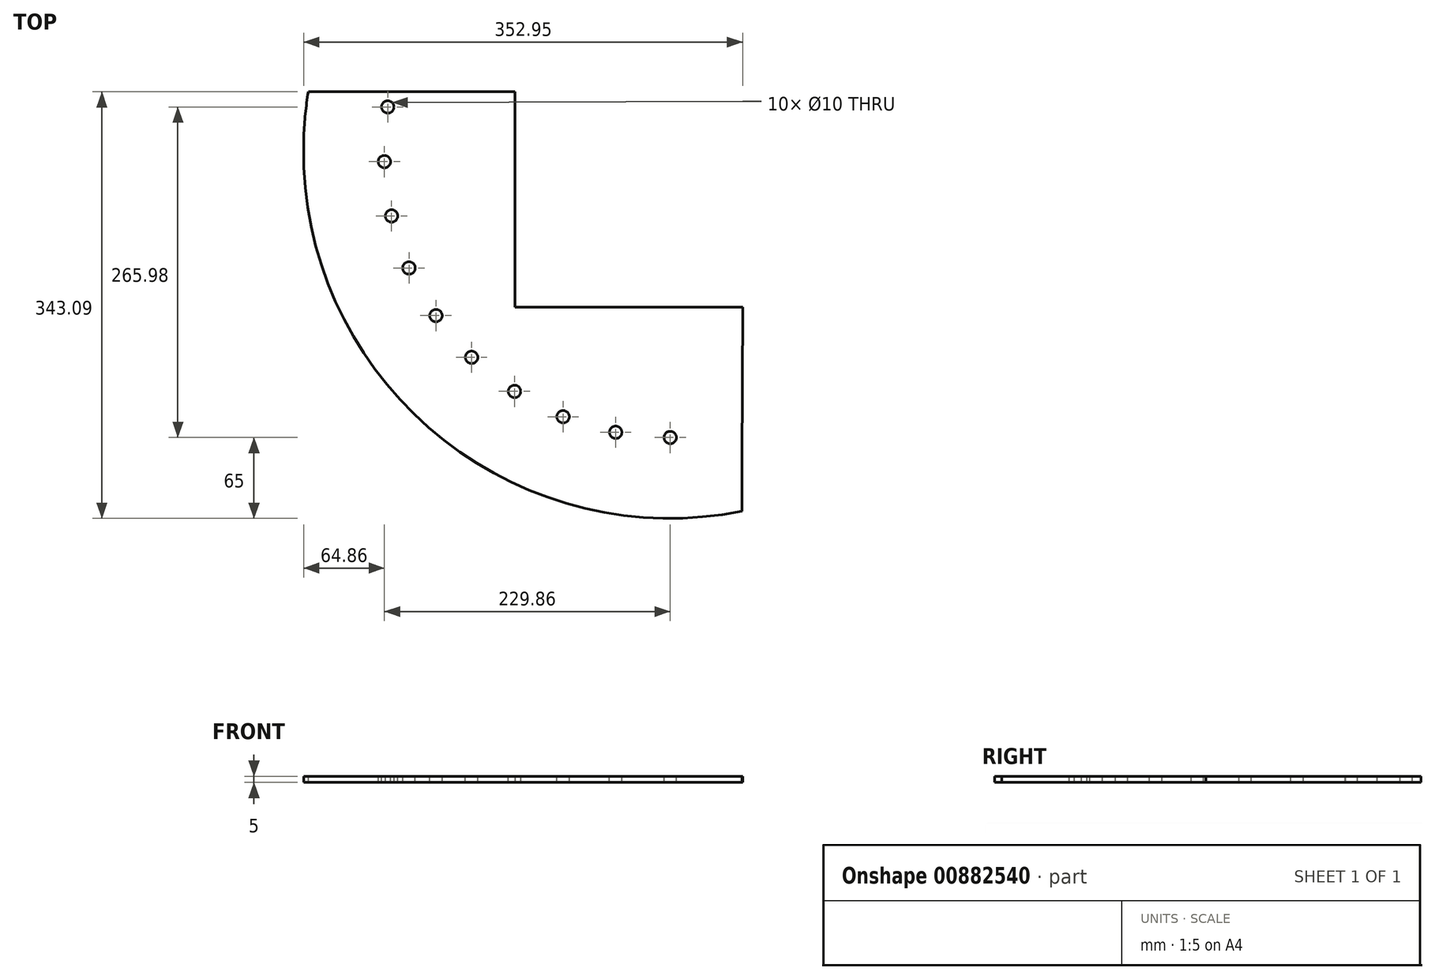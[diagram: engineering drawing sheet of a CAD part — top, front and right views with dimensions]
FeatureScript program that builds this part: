
annotation { "Feature Type Name" : "Feature", "Feature Type Description" : "" }
export const myFeature = defineFeature(function(context is Context, id is Id, definition is map)
    precondition{}
    {
        {
            var Q0;
            Q0=qCreatedBy(makeId("Top.planeOp"),FACE);
            var sketch = newSketch(context, id + "F0", { "sketchPlane" : qUnion([Q0])});
            skLineSegment(sketch, "E0.bottom", {"start": v(125, -125) * mm, "end": v(-125, -125) * mm});
            skLineSegment(sketch, "E0.top", {"start": v(125, 125) * mm, "end": v(-125, 125) * mm});
            skLineSegment(sketch, "E0.left", {"start": v(125, -125) * mm, "end": v(125, 125) * mm});
            skLineSegment(sketch, "E0.right", {"start": v(-125, -125) * mm, "end": v(-125, 125) * mm});
            skPoint(sketch, "E0.middle", {"position": v(0, 0) * mm});
            skLineSegment(sketch, "E1", {"start": v(0, 0) * mm, "end": v(-125, 0) * mm, "construction": true});
            skLineSegment(sketch, "E2.bottom", {"start": v(-349.96, 0) * mm, "end": v(0, 0) * mm});
            skLineSegment(sketch, "E2.left", {"start": v(-349.96, 0) * mm, "end": v(-349.96, 125) * mm});
            skLineSegment(sketch, "E2.right", {"start": v(125, 0) * mm, "end": v(125, 125) * mm});
            skLineSegment(sketch, "E3.MirrorCS", {"start": v(-349.96, 0) * mm, "end": v(-349.96, -249.62) * mm});
            skLineSegment(sketch, "E4.MirrorCS", {"start": v(-349.96, -249.62) * mm, "end": v(125, -249.62) * mm});
            skLineSegment(sketch, "E5.MirrorCS", {"start": v(125, 0) * mm, "end": v(125, -249.62) * mm});
            skLineSegment(sketch, "E6", {"start": v(-349.96, 125) * mm, "end": v(125, 125) * mm});
            skPoint(sketch, "E2.top.start.orphan", {"position": v(-349.96, 249.62) * mm});
            skPoint(sketch, "E7.orphan", {"position": v(125, 249.62) * mm});
            skLineSegment(sketch, "E8", {"start": v(-349.96, 29.15) * mm, "end": v(-125, 29.15) * mm});
            skLineSegment(sketch, "E9", {"start": v(-349.96, -249.62) * mm, "end": v(-349.96, -298.58) * mm});
            skLineSegment(sketch, "E10", {"start": v(-349.96, -298.58) * mm, "end": v(124.79, -298.58) * mm});
            skLineSegment(sketch, "E11", {"start": v(124.79, -298.58) * mm, "end": v(125, -249.62) * mm});
            skLineSegment(sketch, "E12", {"start": v(-294.72, 29.15) * mm, "end": v(-294.72, -298.58) * mm});
            skLineSegment(sketch, "E13", {"start": v(-294.72, 29.15) * mm, "end": v(-294.72, 125) * mm});
            skLineSegment(sketch, "E14", {"start": v(-294.72, 125) * mm, "end": v(-294.72, 148.87) * mm});
            skLineSegment(sketch, "E15", {"start": v(-294.72, 148.87) * mm, "end": v(-125.13, 148.87) * mm});
            skLineSegment(sketch, "E16", {"start": v(-125.13, 148.87) * mm, "end": v(-125, 125) * mm});
            skSolve(sketch);
        }
        {
            var Q0;
            {var subQ0=sQuery(id+"F0.wireOp",EDGE,"E8");var subQ1=sQuery(id+"F0.wireOp",EDGE,"E0.right");var subQ2=makeQuery(id+"F0.imprint","INTERSECT",VERTEX,{"derivedFrom":[subQ1,subQ0]});Q0=makeQuery(id+"F0.imprint","IMPRINT",FACE,{"disambiguationData":[TD([[makeQuery(id+"F0.imprint","IMPRINT",EDGE,{"disambiguationData":[TD([[subQ2,1.0]])],"derivedFrom":subQ1}),1.0]])]});}
            var Q1;
            {var subQ5=sQuery(id+"F0.wireOp",EDGE,"E0.bottom");Q1=makeQuery(id+"F0.imprint","IMPRINT",FACE,{"disambiguationData":[TD([[makeQuery(id+"F0.imprint","IMPRINT",EDGE,{"derivedFrom":subQ5}),1.0]])]});}
            var Q2;
            {var subQ0=sQuery(id+"F0.wireOp",EDGE,"E11");Q2=makeQuery(id+"F0.imprint","IMPRINT",FACE,{"disambiguationData":[TD([[makeQuery(id+"F0.imprint","IMPRINT",EDGE,{"derivedFrom":subQ0}),1.0]])]});}
            var Q3;
            {var subQ4=sQuery(id+"F0.wireOp",EDGE,"E6");var subQ5=sQuery(id+"F0.wireOp",EDGE,"E0.right");var subQ6=makeQuery(id+"F0.imprint","INTERSECT",VERTEX,{"derivedFrom":[subQ5,subQ4]});Q3=makeQuery(id+"F0.imprint","IMPRINT",FACE,{"disambiguationData":[TD([[makeQuery(id+"F0.imprint","IMPRINT",EDGE,{"disambiguationData":[TD([[subQ6,1.0]])],"derivedFrom":subQ5}),1.0]])]});}
            var Q4;
            {var subQ2=sQuery(id+"F0.wireOp",EDGE,"E14");Q4=makeQuery(id+"F0.imprint","IMPRINT",FACE,{"disambiguationData":[TD([[makeQuery(id+"F0.imprint","IMPRINT",EDGE,{"derivedFrom":subQ2}),-1.0]])]});}
            extrude(context, id + "F1", {"entities" : qUnion([Q0, Q1, Q2, Q3, Q4]), "depth" : 5 * mm, "offsetDistance" : 25 * mm});
        }
        {
            var Q0;
            Q0=makeQuery(id+"F1.opExtrude","CAP_FACE",FACE,{"disambiguationData":[OSD([sQuery(id+"F0.wireOp",EDGE,"E0.bottom"),sQuery(id+"F0.wireOp",EDGE,"E0.top"),sQuery(id+"F0.wireOp",EDGE,"E0.left"),sQuery(id+"F0.wireOp",EDGE,"E0.right"),sQuery(id+"F0.wireOp",EDGE,"E2.top"),sQuery(id+"F0.wireOp",EDGE,"E2.left"),sQuery(id+"F0.wireOp",EDGE,"E2.right"),sQuery(id+"F0.wireOp",EDGE,"E3.MirrorCS"),sQuery(id+"F0.wireOp",EDGE,"E4.MirrorCS"),sQuery(id+"F0.wireOp",EDGE,"E5.MirrorCS")])],"isStart":false});
            var sketch = newSketch(context, id + "F2", { "sketchPlane" : qUnion([Q0])});
            skCircle(sketch, "E17", {"center": v(0, 0) * mm, "radius": 270 * mm});
            skCircle(sketch, "E18", {"center": v(0, 0) * mm, "radius": 190 * mm});
            skLineSegment(sketch, "E19", {"start": v(0, 0) * mm, "end": v(-270, 0) * mm, "construction": true});
            skCircle(sketch, "E20", {"center": v(0, 0) * mm, "radius": 230 * mm, "construction": true});
            skCircle(sketch, "E21", {"center": v(-216.13, 78.66) * mm, "radius": 40 * mm});
            skCircle(sketch, "E22", {"center": v(0, -230) * mm, "radius": 40 * mm});
            skLineSegment(sketch, "E23", {"start": v(-216.13, 78.66) * mm, "end": v(0, 0) * mm, "construction": true});
            skLineSegment(sketch, "E24", {"start": v(0, 0) * mm, "end": v(0, -230) * mm, "construction": true});
            skCircle(sketch, "E25", {"center": v(-216.13, 78.66) * mm, "radius": 5 * mm});
            skCircle(sketch, "E26.1.0", {"center": v(-227.17, 35.98) * mm, "radius": 5 * mm});
            skCircle(sketch, "E26.2.0", {"center": v(-229.86, -8.03) * mm, "radius": 5 * mm});
            skCircle(sketch, "E26.3.0", {"center": v(-224.1, -51.74) * mm, "radius": 5 * mm});
            skCircle(sketch, "E26.4.0", {"center": v(-210.12, -93.55) * mm, "radius": 5 * mm});
            skCircle(sketch, "E26.5.0", {"center": v(-188.4, -131.92) * mm, "radius": 5 * mm});
            skCircle(sketch, "E26.6.0", {"center": v(-159.77, -165.45) * mm, "radius": 5 * mm});
            skCircle(sketch, "E26.7.0", {"center": v(-125.27, -192.9) * mm, "radius": 5 * mm});
            skCircle(sketch, "E26.8.0", {"center": v(-86.16, -213.25) * mm, "radius": 5 * mm});
            skCircle(sketch, "E26.9.0", {"center": v(-43.89, -225.77) * mm, "radius": 5 * mm});
            skCircle(sketch, "E26.10.0", {"center": v(0, -230) * mm, "radius": 5 * mm});
            skLineSegment(sketch, "E26.anchor1", {"start": v(0, 0) * mm, "end": v(-216.13, 78.66) * mm, "construction": true});
            skSolve(sketch);
        }
        {
            var Q0;
            Q0=makeQuery(id+"F2.imprint","IMPRINT",FACE,{"disambiguationData":[TD([[makeQuery(id+"F2.imprint","IMPRINT",EDGE,{"derivedFrom":sQuery(id+"F2.wireOp",EDGE,"E26.10.0")}),1.0]])]});
            var Q1;
            {var subQ0=sQuery(id+"F2.wireOp",EDGE,"E26.9.0");var subQ1=sQuery(id+"F2.wireOp",EDGE,"E22");var subQ2=makeQuery(id+"F2.imprint","INTERSECT",VERTEX,{"disambiguationData":[OD(0.0)],"derivedFrom":[subQ1,subQ0]});Q1=makeQuery(id+"F2.imprint","IMPRINT",FACE,{"disambiguationData":[TD([[makeQuery(id+"F2.imprint","IMPRINT",EDGE,{"disambiguationData":[TD([[subQ2,-1.0]])],"derivedFrom":subQ1}),-1.0]])]});}
            var Q2;
            Q2=makeQuery(id+"F2.imprint","IMPRINT",FACE,{"disambiguationData":[TD([[makeQuery(id+"F2.imprint","IMPRINT",EDGE,{"derivedFrom":sQuery(id+"F2.wireOp",EDGE,"E26.8.0")}),1.0]])]});
            var Q3;
            Q3=makeQuery(id+"F2.imprint","IMPRINT",FACE,{"disambiguationData":[TD([[makeQuery(id+"F2.imprint","IMPRINT",EDGE,{"derivedFrom":sQuery(id+"F2.wireOp",EDGE,"E26.7.0")}),1.0]])]});
            var Q4;
            Q4=makeQuery(id+"F2.imprint","IMPRINT",FACE,{"disambiguationData":[TD([[makeQuery(id+"F2.imprint","IMPRINT",EDGE,{"derivedFrom":sQuery(id+"F2.wireOp",EDGE,"E26.5.0")}),1.0]])]});
            var Q5;
            Q5=makeQuery(id+"F2.imprint","IMPRINT",FACE,{"disambiguationData":[TD([[makeQuery(id+"F2.imprint","IMPRINT",EDGE,{"derivedFrom":sQuery(id+"F2.wireOp",EDGE,"E26.6.0")}),1.0]])]});
            var Q6;
            Q6=makeQuery(id+"F2.imprint","IMPRINT",FACE,{"disambiguationData":[TD([[makeQuery(id+"F2.imprint","IMPRINT",EDGE,{"derivedFrom":sQuery(id+"F2.wireOp",EDGE,"E26.4.0")}),1.0]])]});
            var Q7;
            Q7=makeQuery(id+"F2.imprint","IMPRINT",FACE,{"disambiguationData":[TD([[makeQuery(id+"F2.imprint","IMPRINT",EDGE,{"derivedFrom":sQuery(id+"F2.wireOp",EDGE,"E26.3.0")}),1.0]])]});
            var Q8;
            Q8=makeQuery(id+"F2.imprint","IMPRINT",FACE,{"disambiguationData":[TD([[makeQuery(id+"F2.imprint","IMPRINT",EDGE,{"derivedFrom":sQuery(id+"F2.wireOp",EDGE,"E26.2.0")}),1.0]])]});
            var Q9;
            {var subQ0=sQuery(id+"F2.wireOp",EDGE,"E26.1.0");var subQ1=sQuery(id+"F2.wireOp",EDGE,"E21");var subQ2=makeQuery(id+"F2.imprint","INTERSECT",VERTEX,{"disambiguationData":[OD(0.0)],"derivedFrom":[subQ1,subQ0]});Q9=makeQuery(id+"F2.imprint","IMPRINT",FACE,{"disambiguationData":[TD([[makeQuery(id+"F2.imprint","IMPRINT",EDGE,{"disambiguationData":[TD([[subQ2,-1.0]])],"derivedFrom":subQ1}),-1.0]])]});}
            var Q10;
            Q10=makeQuery(id+"F2.imprint","IMPRINT",FACE,{"disambiguationData":[TD([[makeQuery(id+"F2.imprint","IMPRINT",EDGE,{"derivedFrom":sQuery(id+"F2.wireOp",EDGE,"E25")}),1.0]])]});
            var Q11;
            {var subQ0=sQuery(id+"F2.wireOp",EDGE,"E26.1.0");var subQ1=sQuery(id+"F2.wireOp",EDGE,"E21");var subQ2=makeQuery(id+"F2.imprint","INTERSECT",VERTEX,{"disambiguationData":[OD(0.0)],"derivedFrom":[subQ1,subQ0]});Q11=makeQuery(id+"F2.imprint","IMPRINT",FACE,{"disambiguationData":[TD([[makeQuery(id+"F2.imprint","IMPRINT",EDGE,{"disambiguationData":[TD([[subQ2,-1.0]])],"derivedFrom":subQ1}),1.0]])]});}
            var Q12;
            {var subQ0=sQuery(id+"F2.wireOp",EDGE,"E26.9.0");var subQ1=sQuery(id+"F2.wireOp",EDGE,"E22");var subQ2=makeQuery(id+"F2.imprint","INTERSECT",VERTEX,{"disambiguationData":[OD(0.0)],"derivedFrom":[subQ1,subQ0]});Q12=makeQuery(id+"F2.imprint","IMPRINT",FACE,{"disambiguationData":[TD([[makeQuery(id+"F2.imprint","IMPRINT",EDGE,{"disambiguationData":[TD([[subQ2,-1.0]])],"derivedFrom":subQ1}),1.0]])]});}
            extrude(context, id + "F3", {"entities" : qUnion([Q0, Q1, Q2, Q3, Q4, Q5, Q6, Q7, Q8, Q9, Q10, Q11, Q12]), "operationType" : NewBodyOperationType.REMOVE, "oppositeDirection" : true, "depth" : 6 * mm, "offsetDistance" : 25 * mm});
        }
        {
            var Q0;
            Q0=makeQuery(id+"F1.opExtrude","CAP_FACE",FACE,{"disambiguationData":[OSD([sQuery(id+"F0.wireOp",EDGE,"E0.bottom"),sQuery(id+"F0.wireOp",EDGE,"E0.right"),sQuery(id+"F0.wireOp",EDGE,"E5.MirrorCS"),sQuery(id+"F0.wireOp",EDGE,"E8"),sQuery(id+"F0.wireOp",EDGE,"E10"),sQuery(id+"F0.wireOp",EDGE,"E11"),sQuery(id+"F0.wireOp",EDGE,"E12")])],"isStart":false});
            var sketch = newSketch(context, id + "F4", { "sketchPlane" : qUnion([Q0])});
            skCircle(sketch, "E27", {"center": v(0, 0) * mm, "radius": 295 * mm});
            skLineSegment(sketch, "E28", {"start": v(178.33, -235) * mm, "end": v(178.33, -361.67) * mm});
            skLineSegment(sketch, "E29", {"start": v(178.33, -361.67) * mm, "end": v(-429.48, -361.67) * mm});
            skLineSegment(sketch, "E30", {"start": v(-429.48, -361.67) * mm, "end": v(-429.48, 76.22) * mm});
            skLineSegment(sketch, "E31", {"start": v(-429.48, 76.22) * mm, "end": v(-284.98, 76.22) * mm});
            skSolve(sketch);
        }
        {
            var Q0;
            {var subQ0=sQuery(id+"F4.wireOp",EDGE,"E27");var subQ1=makeQuery(id+"F1.opExtrude","CAP_EDGE",EDGE,{"disambiguationData":[OSD([sQuery(id+"F0.wireOp",EDGE,"E12")])],"isStart":false});var subQ2=makeQuery(id+"F4.imprint","INTERSECT",VERTEX,{"disambiguationData":[OD(0.0)],"derivedFrom":[subQ1,subQ0]});Q0=makeQuery(id+"F4.imprint","IMPRINT",FACE,{"disambiguationData":[TD([[makeQuery(id+"F4.imprint","IMPRINT",EDGE,{"disambiguationData":[TD([[subQ2,-1.0]])],"derivedFrom":subQ0}),1.0]])]});}
            var Q1;
            {var subQ0=sQuery(id+"F4.wireOp",EDGE,"E27");var subQ1=makeQuery(id+"F1.opExtrude","CAP_EDGE",EDGE,{"disambiguationData":[OSD([sQuery(id+"F0.wireOp",EDGE,"E8")])],"isStart":false});var subQ2=makeQuery(id+"F4.imprint","INTERSECT",VERTEX,{"derivedFrom":[subQ1,subQ0]});Q1=makeQuery(id+"F4.imprint","IMPRINT",FACE,{"disambiguationData":[TD([[makeQuery(id+"F4.imprint","IMPRINT",EDGE,{"disambiguationData":[TD([[subQ2,-1.0]])],"derivedFrom":subQ0}),-1.0]])]});}
            var Q2;
            {var subQ11=sQuery(id+"F4.wireOp",EDGE,"E28");Q2=makeQuery(id+"F4.imprint","IMPRINT",FACE,{"disambiguationData":[TD([[makeQuery(id+"F4.imprint","IMPRINT",EDGE,{"derivedFrom":subQ11}),-1.0]])]});}
            var Q3;
            {var subQ5=makeQuery(id+"F1.opExtrude","CAP_EDGE",EDGE,{"disambiguationData":[OSD([sQuery(id+"F0.wireOp",EDGE,"E10")])],"isStart":false});Q3=makeQuery(id+"F4.imprint","IMPRINT",FACE,{"disambiguationData":[TD([[makeQuery(id+"F4.imprint","IMPRINT",EDGE,{"derivedFrom":subQ5}),1.0]])]});}
            var Q4;
            {var subQ0=sQuery(id+"F4.wireOp",EDGE,"E31");var subQ1=sQuery(id+"F4.wireOp",EDGE,"E27");var subQ2=makeQuery(id+"F4.imprint","INTERSECT",VERTEX,{"derivedFrom":[subQ1,subQ0]});Q4=makeQuery(id+"F4.imprint","IMPRINT",FACE,{"disambiguationData":[TD([[makeQuery(id+"F4.imprint","IMPRINT",EDGE,{"disambiguationData":[TD([[subQ2,-1.0]])],"derivedFrom":subQ1}),-1.0]])]});}
            var Q5;
            {var subQ0=sQuery(id+"F4.wireOp",EDGE,"E31");var subQ1=sQuery(id+"F4.wireOp",EDGE,"E27");var subQ2=makeQuery(id+"F4.imprint","INTERSECT",VERTEX,{"derivedFrom":[subQ1,subQ0]});Q5=makeQuery(id+"F4.imprint","IMPRINT",FACE,{"disambiguationData":[TD([[makeQuery(id+"F4.imprint","IMPRINT",EDGE,{"disambiguationData":[TD([[subQ2,1.0]])],"derivedFrom":subQ1}),-1.0]])]});}
            extrude(context, id + "F5", {"entities" : qUnion([Q0, Q1, Q2, Q3, Q4, Q5]), "operationType" : NewBodyOperationType.REMOVE, "oppositeDirection" : true, "depth" : 25 * mm, "offsetDistance" : 25 * mm});
        }
        {
            var Q0;
            Q0=makeQuery(id+"F1.opExtrude","CAP_FACE",FACE,{"disambiguationData":[OSD([sQuery(id+"F0.wireOp",EDGE,"E0.bottom"),sQuery(id+"F0.wireOp",EDGE,"E0.right"),sQuery(id+"F0.wireOp",EDGE,"E5.MirrorCS"),sQuery(id+"F0.wireOp",EDGE,"E10"),sQuery(id+"F0.wireOp",EDGE,"E11"),sQuery(id+"F0.wireOp",EDGE,"E12"),sQuery(id+"F0.wireOp",EDGE,"E13"),sQuery(id+"F0.wireOp",EDGE,"E14"),sQuery(id+"F0.wireOp",EDGE,"E15"),sQuery(id+"F0.wireOp",EDGE,"E16")])],"isStart":false});
            var sketch = newSketch(context, id + "F6", { "sketchPlane" : qUnion([Q0])});
            skLineSegment(sketch, "E32", {"start": v(-125.13, 148.87) * mm, "end": v(-307.53, 160.18) * mm});
            skLineSegment(sketch, "E33", {"start": v(-307.53, 160.18) * mm, "end": v(-291.05, 48.09) * mm});
            skLineSegment(sketch, "E34", {"start": v(125, -249.62) * mm, "end": v(-159.16, -248.38) * mm});
            skLineSegment(sketch, "E35", {"start": v(-152.95, -283.8) * mm, "end": v(-36.66, -298.73) * mm});
            skLineSegment(sketch, "E36", {"start": v(-36.66, -298.73) * mm, "end": v(96.4, -298.73) * mm});
            skLineSegment(sketch, "E37", {"start": v(96.4, -298.73) * mm, "end": v(143.24, -276.33) * mm});
            skLineSegment(sketch, "E38", {"start": v(143.24, -276.33) * mm, "end": v(125, -249.62) * mm});
            skLineSegment(sketch, "E39", {"start": v(57.69, -249.33) * mm, "end": v(58.34, -100.5) * mm});
            skLineSegment(sketch, "E40", {"start": v(58.34, -100.5) * mm, "end": v(147.99, -100.9) * mm});
            skLineSegment(sketch, "E41", {"start": v(147.99, -100.9) * mm, "end": v(143.24, -276.33) * mm});
            skLineSegment(sketch, "E42", {"start": v(-291.05, 48.09) * mm, "end": v(-111.17, 48.09) * mm});
            skLineSegment(sketch, "E43", {"start": v(-111.17, 48.09) * mm, "end": v(-104.12, 144.52) * mm});
            skLineSegment(sketch, "E44", {"start": v(-104.12, 144.52) * mm, "end": v(-121.12, 152) * mm});
            skLineSegment(sketch, "E45", {"start": v(-121.12, 152) * mm, "end": v(-125.13, 148.87) * mm});
            skLineSegment(sketch, "E46", {"start": v(-159.16, -248.38) * mm, "end": v(-152.95, -283.8) * mm});
            skLineSegment(sketch, "E47", {"start": v(57.69, -249.33) * mm, "end": v(57.69, -298.73) * mm});
            skSolve(sketch);
        }
        {
            var Q0;
            Q0=makeQuery(id+"F6.imprint","IMPRINT",FACE,{"disambiguationData":[TD([[makeQuery(id+"F6.imprint","IMPRINT",EDGE,{"derivedFrom":makeQuery(id+"F3.boolean.opBoolean","COPY",EDGE,{"derivedFrom":makeQuery(id+"F3.opExtrude","CAP_EDGE",EDGE,{"disambiguationData":[OSD([sQuery(id+"F2.wireOp",EDGE,"E25")])],"isStart":true})})}),1.0]])]});
            var Q1;
            Q1=makeQuery(id+"F6.imprint","IMPRINT",FACE,{"disambiguationData":[TD([[makeQuery(id+"F6.imprint","IMPRINT",EDGE,{"derivedFrom":sQuery(id+"F6.wireOp",EDGE,"E32")}),1.0]])]});
            var Q2;
            {var subQ0=sQuery(id+"F6.wireOp",EDGE,"E43");Q2=makeQuery(id+"F6.imprint","IMPRINT",FACE,{"disambiguationData":[TD([[makeQuery(id+"F6.imprint","IMPRINT",EDGE,{"derivedFrom":subQ0}),1.0]])]});}
            var Q3;
            {var subQ8=sQuery(id+"F6.wireOp",EDGE,"E35");Q3=makeQuery(id+"F6.imprint","IMPRINT",FACE,{"disambiguationData":[TD([[makeQuery(id+"F6.imprint","IMPRINT",EDGE,{"derivedFrom":subQ8}),1.0]])]});}
            var Q4;
            Q4=makeQuery(id+"F6.imprint","IMPRINT",FACE,{"disambiguationData":[TD([[makeQuery(id+"F6.imprint","IMPRINT",EDGE,{"derivedFrom":sQuery(id+"F6.wireOp",EDGE,"E38")}),-1.0]])]});
            var Q5;
            {var subQ8=sQuery(id+"F6.wireOp",EDGE,"E37");Q5=makeQuery(id+"F6.imprint","IMPRINT",FACE,{"disambiguationData":[TD([[makeQuery(id+"F6.imprint","IMPRINT",EDGE,{"derivedFrom":subQ8}),1.0]])]});}
            var Q6;
            {var subQ2=makeQuery(id+"F1.opExtrude","CAP_EDGE",EDGE,{"disambiguationData":[OSD([sQuery(id+"F0.wireOp",EDGE,"E16")])],"isStart":false});Q6=makeQuery(id+"F6.imprint","IMPRINT",FACE,{"disambiguationData":[TD([[makeQuery(id+"F6.imprint","IMPRINT",EDGE,{"derivedFrom":subQ2}),-1.0]])]});}
            var Q7;
            {var subQ1=makeQuery(id+"F1.opExtrude","CAP_EDGE",EDGE,{"disambiguationData":[OSD([sQuery(id+"F0.wireOp",EDGE,"E11")])],"isStart":false});var subQ2=subQ1;Q7=makeQuery(id+"F6.imprint","IMPRINT",FACE,{"disambiguationData":[TD([[makeQuery(id+"F6.imprint","IMPRINT",EDGE,{"derivedFrom":subQ2}),1.0]])]});}
            var Q8;
            {var subQ1=makeQuery(id+"F1.opExtrude","CAP_EDGE",EDGE,{"disambiguationData":[OSD([sQuery(id+"F0.wireOp",EDGE,"E5.MirrorCS")])],"isStart":false});Q8=makeQuery(id+"F6.imprint","IMPRINT",FACE,{"disambiguationData":[TD([[makeQuery(id+"F6.imprint","IMPRINT",EDGE,{"derivedFrom":subQ1}),-1.0]])]});}
            extrude(context, id + "F7", {"entities" : qUnion([Q0, Q1, Q2, Q3, Q4, Q5, Q6, Q7, Q8]), "operationType" : NewBodyOperationType.REMOVE, "oppositeDirection" : true, "depth" : 25 * mm, "offsetDistance" : 25 * mm});
        }
    });
